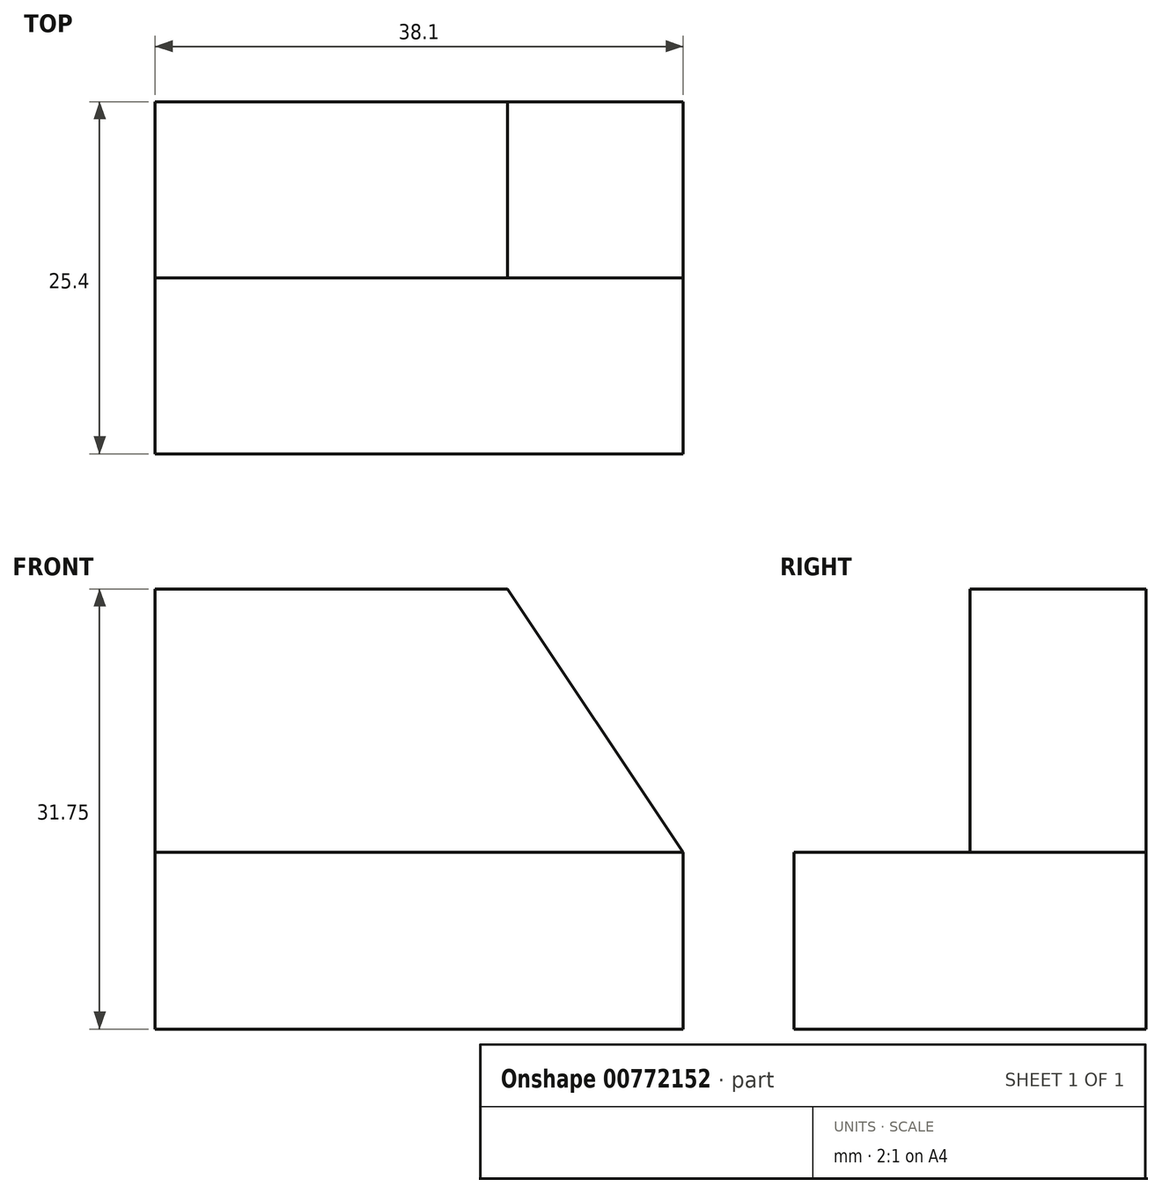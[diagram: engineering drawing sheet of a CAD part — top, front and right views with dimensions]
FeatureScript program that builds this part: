
annotation { "Feature Type Name" : "Feature", "Feature Type Description" : "" }
export const myFeature = defineFeature(function(context is Context, id is Id, definition is map)
    precondition{}
    {
        {
            var Q0;
            Q0=qCreatedBy(makeId("Front.planeOp"),FACE);
            var sketch = newSketch(context, id + "F0", { "sketchPlane" : qUnion([Q0])});
            skLineSegment(sketch, "E0", {"start": v(0, 0) * mm, "end": v(0, 31.75) * mm});
            skLineSegment(sketch, "E1", {"start": v(0, 31.75) * mm, "end": v(38.1, 31.75) * mm});
            skLineSegment(sketch, "E2", {"start": v(38.1, 31.75) * mm, "end": v(38.1, 0) * mm});
            skLineSegment(sketch, "E3", {"start": v(0, 0) * mm, "end": v(38.1, 0) * mm});
            skSolve(sketch);
        }
        {
            var Q0;
            Q0=qCreatedBy(makeId("Front.planeOp"),FACE);
            var sketch = newSketch(context, id + "F1", { "sketchPlane" : qUnion([Q0])});
            skLineSegment(sketch, "E4", {"start": v(0, 28.39) * mm, "end": v(0, 0) * mm});
            skLineSegment(sketch, "E5", {"start": v(0, 0) * mm, "end": v(34.04, 0) * mm});
            skLineSegment(sketch, "E6", {"start": v(0, 28.39) * mm, "end": v(34.04, 28.39) * mm});
            skLineSegment(sketch, "E7", {"start": v(33.82, 28.82) * mm, "end": v(34.04, 0) * mm});
            skSolve(sketch);
        }
        {
            var Q0;
            Q0 = qSketchRegion(id + "F1", true);
            extrude(context, id + "F2", {"entities" : qUnion([Q0]), "depth" : 25.4 * mm, "offsetDistance" : 25.4 * mm});
        }
        {
            var Q0;
            Q0 = qSketchRegion(id + "F0", true);
            extrude(context, id + "F3", {"entities" : qUnion([Q0]), "operationType" : NewBodyOperationType.ADD, "depth" : 25.4 * mm, "offsetDistance" : 25.4 * mm});
        }
        {
            var Q0;
            Q0=makeQuery(id+"F3.boolean.opBoolean","MERGE",FACE,{"derivedFrom":[makeQuery(id+"F2.opExtrude","CAP_FACE",FACE,{"disambiguationData":[OSD([sQuery(id+"F1.wireOp",EDGE,"E4"),sQuery(id+"F1.wireOp",EDGE,"E5"),sQuery(id+"F1.wireOp",EDGE,"E6"),sQuery(id+"F1.wireOp",EDGE,"E7")])],"isStart":false}),makeQuery(id+"F3.opExtrude","CAP_FACE",FACE,{"disambiguationData":[OSD([sQuery(id+"F0.wireOp",EDGE,"E0"),sQuery(id+"F0.wireOp",EDGE,"E1"),sQuery(id+"F0.wireOp",EDGE,"E2"),sQuery(id+"F0.wireOp",EDGE,"E3")])],"isStart":false})]});
            var sketch = newSketch(context, id + "F4", { "sketchPlane" : qUnion([Q0])});
            skLineSegment(sketch, "E8", {"start": v(0, 0) * mm, "end": v(0, 12.77) * mm});
            skLineSegment(sketch, "E9", {"start": v(0, 12.77) * mm, "end": v(38.1, 12.77) * mm});
            skSolve(sketch);
        }
        {
            var Q0;
            {var subQ0=sQuery(id+"F4.wireOp",EDGE,"E9");Q0=makeQuery(id+"F4.imprint","IMPRINT",FACE,{"disambiguationData":[TD([[makeQuery(id+"F4.imprint","IMPRINT",EDGE,{"derivedFrom":subQ0}),1.0]])]});}
            extrude(context, id + "F5", {"entities" : qUnion([Q0]), "operationType" : NewBodyOperationType.REMOVE, "oppositeDirection" : true, "depth" : 12.7 * mm, "offsetDistance" : 25.4 * mm});
        }
        {
            var Q0;
            Q0=makeQuery(id+"F5.boolean.opBoolean","COPY",FACE,{"derivedFrom":makeQuery(id+"F5.opExtrude","CAP_FACE",FACE,{"disambiguationData":[OSD([sQuery(id+"F0.wireOp",EDGE,"E0"),sQuery(id+"F0.wireOp",EDGE,"E1"),sQuery(id+"F0.wireOp",EDGE,"E2"),sQuery(id+"F1.wireOp",EDGE,"E4"),sQuery(id+"F4.wireOp",EDGE,"E9")])],"isStart":false})});
            var sketch = newSketch(context, id + "F6", { "sketchPlane" : qUnion([Q0])});
            skLineSegment(sketch, "E10", {"start": v(0, 31.75) * mm, "end": v(25.43, 31.75) * mm});
            skLineSegment(sketch, "E11", {"start": v(25.43, 31.75) * mm, "end": v(38.1, 12.77) * mm});
            skSolve(sketch);
        }
        {
            var Q0;
            {var subQ0=sQuery(id+"F6.wireOp",EDGE,"E11");Q0=makeQuery(id+"F6.imprint","IMPRINT",FACE,{"disambiguationData":[TD([[makeQuery(id+"F6.imprint","IMPRINT",EDGE,{"derivedFrom":subQ0}),1.0]])]});}
            extrude(context, id + "F7", {"entities" : qUnion([Q0]), "operationType" : NewBodyOperationType.REMOVE, "endBound" : BoundingType.THROUGH_ALL, "oppositeDirection" : true, "depth" : 25.4 * mm, "offsetDistance" : 25.4 * mm});
        }
    });
